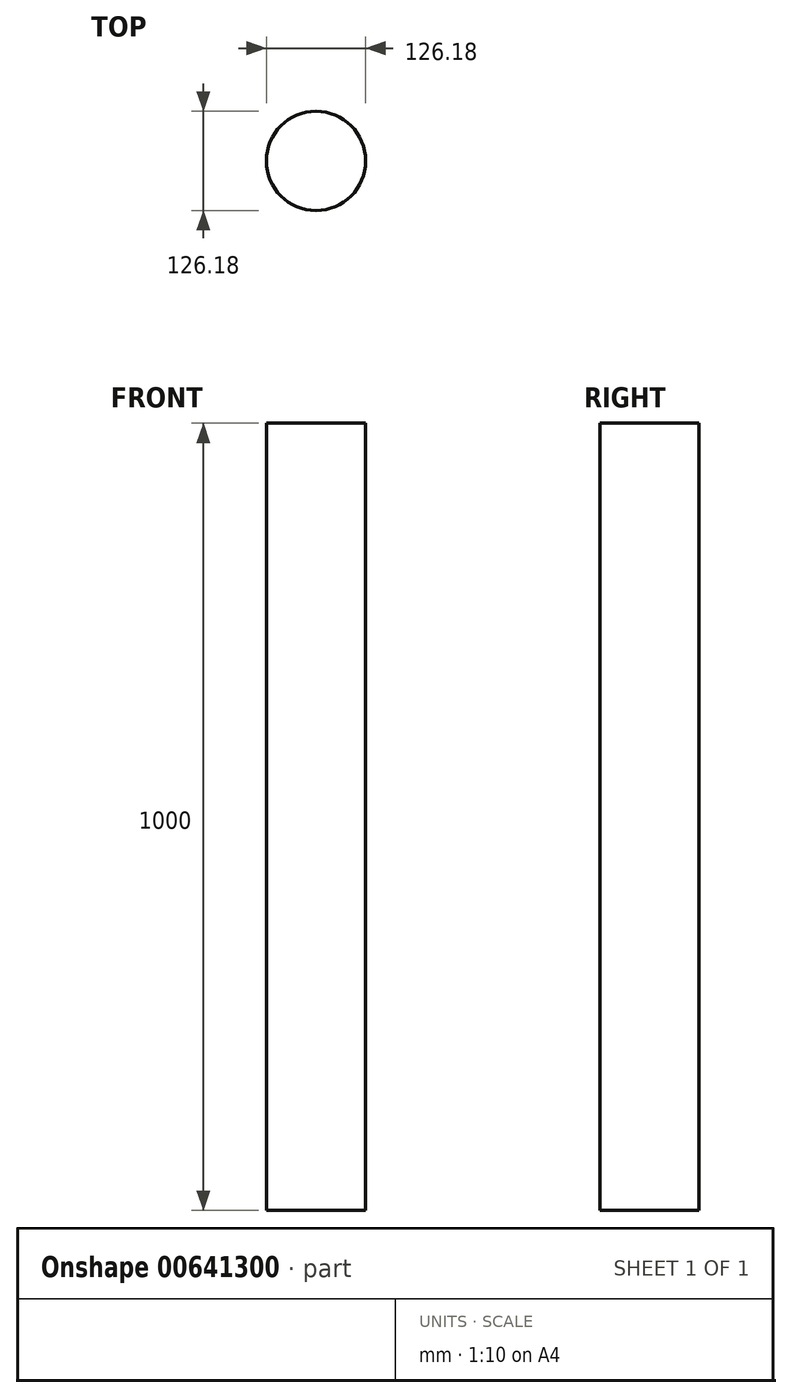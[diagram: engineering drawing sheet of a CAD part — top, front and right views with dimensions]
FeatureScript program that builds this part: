
annotation { "Feature Type Name" : "Feature", "Feature Type Description" : "" }
export const myFeature = defineFeature(function(context is Context, id is Id, definition is map)
    precondition{}
    {
        {
            var Q0;
            Q0=qCreatedBy(makeId("Top.planeOp"),FACE);
            var sketch = newSketch(context, id + "F0", { "sketchPlane" : qUnion([Q0])});
            skCircle(sketch, "E0", {"center": v(0, -1.33) * mm, "radius": 63.09 * mm});
            skSolve(sketch);
        }
        {
            var Q0;
            Q0 = qSketchRegion(id + "F0", true);
            extrude(context, id + "F1", {"entities" : qUnion([Q0]), "depth" : 1000 * mm, "offsetDistance" : 25.4 * mm});
        }
    });
